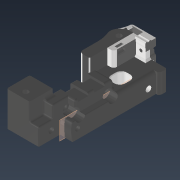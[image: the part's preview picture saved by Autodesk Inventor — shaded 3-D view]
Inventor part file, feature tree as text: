
AUTODESK INVENTOR PART (.ipt)
format: ipt  version: 2022.1 (Build 261234020, 234B)  size: 2,312,704 bytes
history: native  units: mm
features: delete_face x29, extrude x16, sketch x16, fillet x9, projected_geometry x7, other x6, chamfer x5, direct_edit x4, move_body x4, reference x2, plane x1
ambient origin geometry x8: Origin, YZ Plane, XZ Plane, XY Plane, X Axis, Y Axis, Z Axis, Center Point
bodies: Volumenkörper1 (feature_tree)
feature tree (99):
  other  "Baugruppe265_left.iam"
  other  "x_carriage_frame_left.ipt:1"
  other  "Bauteil2859.ipt:1"
  delete_face  "Fläche löschen1"
  delete_face  "Fläche löschen2"
  delete_face  "Fläche löschen3"
  delete_face  "Fläche löschen4"
  extrude  "Extrusion1"  Depth=10.0mm
  extrude  "Extrusion2"  TaperAngle=0.0deg  [1 undecoded]
  delete_face  "Fläche löschen5"
  delete_face  "Fläche löschen6"
  delete_face  "Fläche löschen7"
  delete_face  "Fläche löschen8"
  delete_face  "Fläche löschen9"
  delete_face  "Fläche löschen10"
  delete_face  "Fläche löschen11"
  extrude  "Extrusion3"  Depth=10.0mm
  direct_edit  "Direktbearbeitung1"
  chamfer  "Fase1"  Distance=10.0mm
  delete_face  "Fläche löschen12"
  delete_face  "Fläche löschen13"
  extrude  "Extrusion4"  Depth=0.4mm TaperAngle=45.0deg
  delete_face  "Fläche löschen14"
  delete_face  "Fläche löschen15"
  fillet  "Rundung1"  [1 undecoded]
  fillet  "Rundung2"  Radius=10.0mm
  fillet  "Rundung3"  Radius=5.0mm
  fillet  "Rundung4"  Radius=15.0mm
  delete_face  "Fläche löschen16"
  extrude  "Extrusion5"  Depth=1.0mm
  delete_face  "Fläche löschen17"
  fillet  "Rundung5"  Radius=0.5mm
  chamfer  "Fase2"  Distance=0.4mm Angle=45.0deg
  extrude  "Extrusion6"  Depth=3.0mm TaperAngle=0.0deg
  direct_edit  "Direktbearbeitung2"
  fillet  "Rundung6"  Radius=2.0mm
  fillet  "Rundung7"  Radius=0.5mm
  extrude  "Extrusion7"  Depth=0.6mm TaperAngle=0.0deg
  delete_face  "Fläche löschen18"
  extrude  "Extrusion8"  TaperAngle=45.0deg  [1 undecoded]
  delete_face  "Fläche löschen19"
  extrude  "Extrusion9"  Depth=0.6mm
  fillet  "Rundung8"  Radius=0.41mm
  chamfer  "Fase3"  Distance=0.6mm
  extrude  "Extrusion10"  Depth=3.0mm
  delete_face  "Fläche löschen20"
  delete_face  "Fläche löschen21"
  direct_edit  "Direktbearbeitung3"
  delete_face  "Fläche löschen22"
  delete_face  "Fläche löschen23"
  delete_face  "Fläche löschen24"
  delete_face  "Fläche löschen25"
  delete_face  "Fläche löschen26"
  extrude  "Extrusion11"  Depth=3.0mm
  fillet  "Rundung9"  [1 undecoded]
  chamfer  "Fase4"  Distance=0.4mm Angle=45.0deg
  delete_face  "Fläche löschen27"
  delete_face  "Fläche löschen28"
  extrude  "Extrusion12"  Depth=10.0mm TaperAngle=0.0deg
  extrude  "Extrusion13"  Depth=10.0mm TaperAngle=0.0deg
  extrude  "Extrusion14"  Depth=10.0mm
  plane  "Arbeitsebene1"
  extrude  "Extrusion15"  Depth=1.0mm TaperAngle=45.0deg
  chamfer  "Fase5"  Distance=2.6mm
  extrude  "Extrusion16"  Depth=10.0mm
  direct_edit  "Direktbearbeitung5"
  delete_face  "Fläche löschen29"
  sketch  "Skizze1"  dims[d0=10.0mm d1=2.02mm]
  sketch  "Skizze2"  dims[d2=10.0mm d3=0.0mm d4=0.0mm]
  sketch  "Skizze3"  dims[d5=0.0mm d6=0.0mm d7=6.0mm d8=10.0mm d9=0.0mm]
  projected_geometry  "Projizierte Kontur1"
  sketch  "Skizze4"  dims[d10=0.0mm d11=0.0mm d12=1.49mm d13=0.4mm d14=2.0mm d15=45.0deg d16=30.0deg d17=10.0mm d18=0.0mm d19=5.0mm d20=15.0mm]
  sketch  "Skizze5"  dims[d21=1.0mm d22=20.0mm d23=0.5mm d24=0.0mm]
  projected_geometry  "Projizierte Kontur2"
  sketch  "Skizze6"  dims[d25=2.0mm d26=0.4mm d27=2.0mm d28=45.0deg]
  projected_geometry  "Projizierte Kontur3"
  sketch  "Skizze7"  dims[d29=3.0mm d30=0.5mm d31=0.0mm]
  projected_geometry  "Projizierte Kontur4"
  sketch  "Skizze8"  dims[d32=0.0mm d33=0.0mm d34=-2.0mm d35=2.0mm d36=0.5mm]
  sketch  "Skizze9"  dims[d37=1.0mm d38=0.6mm d39=0.0mm]
  projected_geometry  "Projizierte Kontur5"
  sketch  "Skizze10"  dims[d40=45.0deg d41=45.0deg]
  sketch  "Skizze11"  dims[d42=0.472556mm d43=0.41mm d44=0.41mm d45=0.6mm d46=0.0mm]
  projected_geometry  "Projizierte Kontur6"
  sketch  "Skizze12"  dims[d47=3.0mm d48=4.0mm]
  projected_geometry  "Projizierte Kontur7"
  reference  "Referenz1"
  reference  "Referenz2"
  sketch  "Skizze13"  dims[d49=3.0mm d50=3.0mm d51=0.0mm d52=0.0mm]
  sketch  "Skizze14"  dims[d53=3.0mm d54=0.4mm d55=2.0mm d56=45.0deg]
  sketch  "Skizze15"  dims[d57=2.2mm d58=10.0mm d59=0.0mm]
  sketch  "Skizze16"  dims[d60=0.0mm d61=0.0mm d62=5.76mm d66=10.0mm d67=0.0mm d68=2.0mm d69=1.0mm d70=2.0mm d71=45.0deg d72=2.6mm d73=1.505mm d74=1.505mm d75=10.0mm d76=0.0mm d77=1.601mm d78=10.0mm d79=0.0mm d80=1.601mm d81=10.0mm d82=0.0mm d83=-5.0mm d84=5.6mm d85=5.6mm d86=2.8mm d87=30.0deg d88=2.6mm d89=0.0mm d90=0.4mm d91=2.0mm d92=45.0deg d93=3.4mm d94=10.0mm d95=0.0mm d96=0.0mm d97=0.0mm d98=-3.0mm]
  move_body  "Verschieben1"
  move_body  "Verschieben2"
  move_body  "Verschieben3"
  other  "<userpath>\Desktop\RAMA_SBNG\Klicky\Carriage_NG.iam"
  other  "Carriage_NG.iam"
  other  "6x3 Magnet:1"
  move_body  "Verschieben5"
note: 4 required parameter values undecoded (feature->parameter linkage not recoverable at this tier; creation-order binding heuristic only, values carry confidence <= 0.55)
